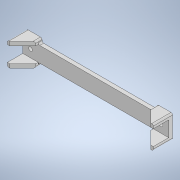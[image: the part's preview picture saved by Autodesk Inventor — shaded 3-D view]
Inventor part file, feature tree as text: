
AUTODESK INVENTOR PART (.ipt)
format: ipt  version: 2022 (Build 260153000, 153)  size: 156,160 bytes
history: native  units: mm
features: extrude x2, plane x2, fillet x2, mirror x2, sketch x1, hole x1, chamfer x1
ambient origin geometry x8: Origin, YZ Plane, XZ Plane, XY Plane, X Axis, Y Axis, Z Axis, Center Point
bodies: Solid1 (feature_tree)
feature tree (11):
  sketch  "Sketch1"  dims[d0=169.8625mm d1=20.0mm d2=10.0mm d3=10.0mm d4=10.0mm d5=5.0mm d6=0.0mm d7=5.0mm d8=6.0mm d9=6.5024mm d10=3.4036mm d11=14.3117mm d12=8.0mm d13=20.594885mm d14=20.0mm d15=5.0mm d16=25.0mm d17=0.0mm d18=16.75mm d19=2.0mm d20=45.0deg d21=2.0mm d22=2.0mm]
  extrude  "Extrusion1"  Depth=20.0mm
  hole  "Hole1"  [1 undecoded]
  extrude  "Extrusion2"  Depth=10.0mm
  plane  "Work Plane1"
  plane  "Work Plane2"
  chamfer  "Chamfer1"  Distance=10.0mm
  fillet  "Fillet1"  Radius=5.0mm
  mirror  "Mirror1"
  mirror  "Mirror2"
  fillet  "Fillet2"  Radius=20.0mm
note: 1 required parameter value undecoded (feature->parameter linkage not recoverable at this tier; creation-order binding heuristic only, values carry confidence <= 0.55)
